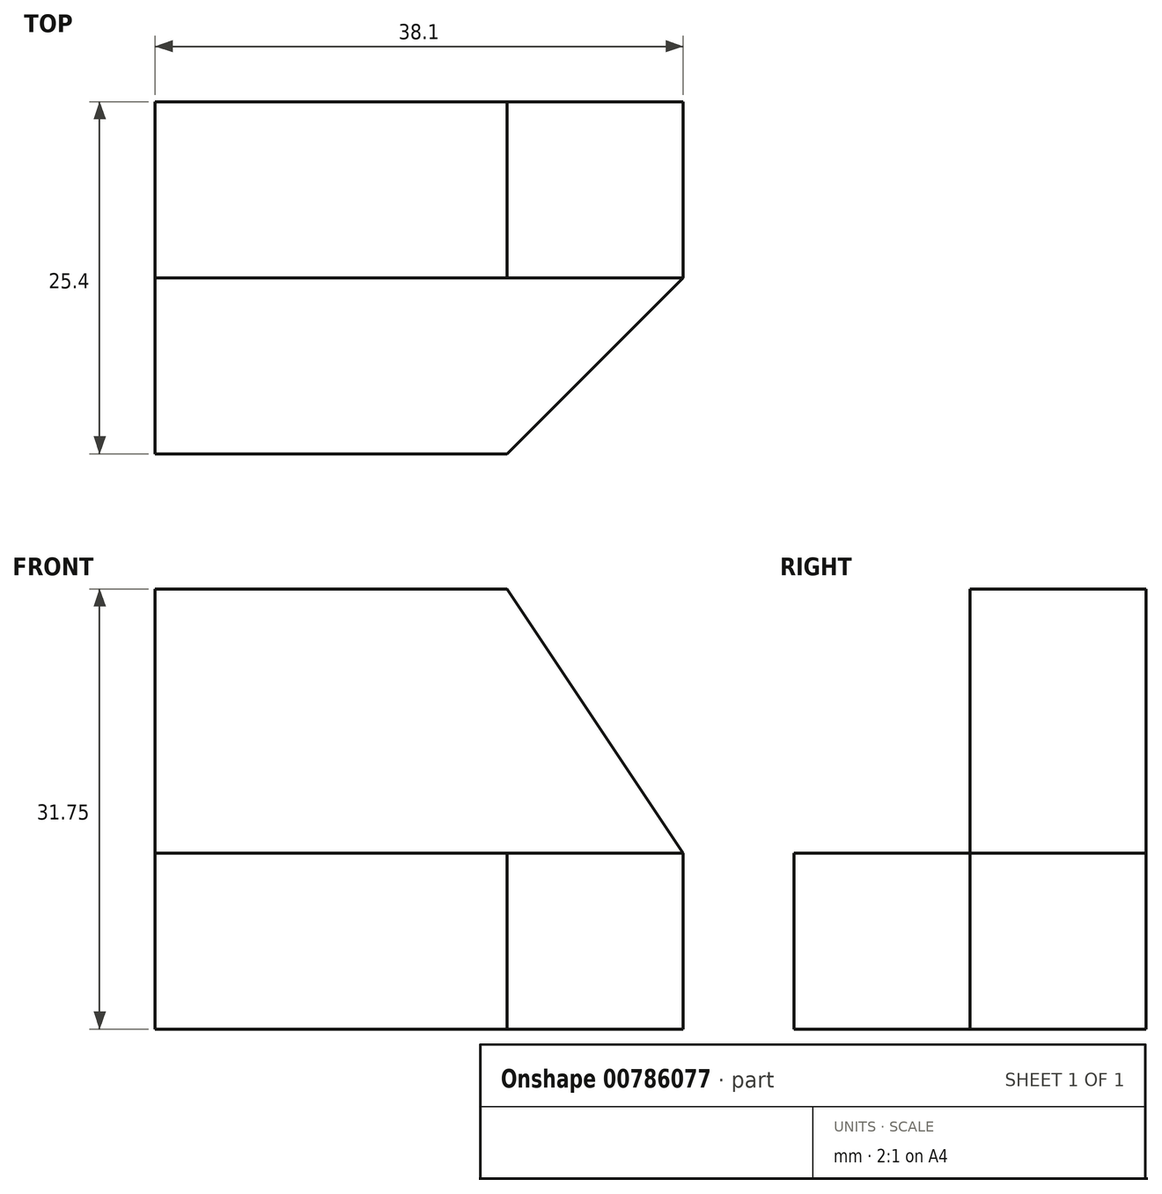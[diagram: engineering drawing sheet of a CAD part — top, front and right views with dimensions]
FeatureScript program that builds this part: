
annotation { "Feature Type Name" : "Feature", "Feature Type Description" : "" }
export const myFeature = defineFeature(function(context is Context, id is Id, definition is map)
    precondition{}
    {
        {
            var Q0;
            Q0=qCreatedBy(makeId("Front.planeOp"),FACE);
            var sketch = newSketch(context, id + "F0", { "sketchPlane" : qUnion([Q0])});
            skLineSegment(sketch, "E0", {"start": v(0, 0) * mm, "end": v(38.1, 0) * mm});
            skLineSegment(sketch, "E1", {"start": v(38.1, 0) * mm, "end": v(38.1, 31.75) * mm});
            skLineSegment(sketch, "E2", {"start": v(38.1, 31.75) * mm, "end": v(0, 31.75) * mm});
            skLineSegment(sketch, "E3", {"start": v(0, 31.75) * mm, "end": v(0, 0) * mm});
            skSolve(sketch);
        }
        {
            var Q0;
            Q0=makeQuery(id+"F0.imprint","IMPRINT",FACE,{"disambiguationData":[TD([[makeQuery(id+"F0.imprint","IMPRINT",EDGE,{"derivedFrom":sQuery(id+"F0.wireOp",EDGE,"E0")}),1.0]])]});
            extrude(context, id + "F1", {"entities" : qUnion([Q0]), "depth" : 25.4 * mm, "offsetDistance" : 25.4 * mm});
        }
        {
            var Q0;
            Q0=makeQuery(id+"F1.opExtrude","SWEPT_FACE",FACE,{"disambiguationData":[OSD([sQuery(id+"F0.wireOp",EDGE,"E1")])]});
            var sketch = newSketch(context, id + "F2", { "sketchPlane" : qUnion([Q0])});
            skLineSegment(sketch, "E4", {"start": v(-25.4, 0) * mm, "end": v(-25.4, 12.7) * mm});
            skLineSegment(sketch, "E5", {"start": v(-25.4, 12.7) * mm, "end": v(-12.7, 12.7) * mm});
            skLineSegment(sketch, "E6", {"start": v(-12.7, 12.7) * mm, "end": v(-12.7, 31.75) * mm});
            skSolve(sketch);
        }
        {
            var Q0;
            {var subQ0=sQuery(id+"F2.wireOp",EDGE,"E5");Q0=makeQuery(id+"F2.imprint","IMPRINT",FACE,{"disambiguationData":[TD([[makeQuery(id+"F2.imprint","IMPRINT",EDGE,{"derivedFrom":subQ0}),1.0]])]});}
            extrude(context, id + "F3", {"entities" : qUnion([Q0]), "operationType" : NewBodyOperationType.REMOVE, "oppositeDirection" : true, "depth" : 38.1 * mm, "offsetDistance" : 25.4 * mm});
        }
        {
            var Q0;
            Q0=makeQuery(id+"F3.boolean.opBoolean","COPY",FACE,{"derivedFrom":makeQuery(id+"F3.opExtrude","SWEPT_FACE",FACE,{"disambiguationData":[OSD([sQuery(id+"F2.wireOp",EDGE,"E6")])]})});
            var sketch = newSketch(context, id + "F4", { "sketchPlane" : qUnion([Q0])});
            skLineSegment(sketch, "E7", {"start": v(0, 31.75) * mm, "end": v(25.4, 31.75) * mm});
            skLineSegment(sketch, "E8", {"start": v(25.4, 31.75) * mm, "end": v(38.1, 12.7) * mm});
            skSolve(sketch);
        }
        {
            var Q0;
            {var subQ0=sQuery(id+"F4.wireOp",EDGE,"E8");Q0=makeQuery(id+"F4.imprint","IMPRINT",FACE,{"disambiguationData":[TD([[makeQuery(id+"F4.imprint","IMPRINT",EDGE,{"derivedFrom":subQ0}),1.0]])]});}
            extrude(context, id + "F5", {"entities" : qUnion([Q0]), "operationType" : NewBodyOperationType.REMOVE, "oppositeDirection" : true, "depth" : 12.7 * mm, "offsetDistance" : 25.4 * mm});
        }
        {
            var Q0;
            Q0=makeQuery(id+"F3.boolean.opBoolean","COPY",FACE,{"derivedFrom":makeQuery(id+"F3.opExtrude","SWEPT_FACE",FACE,{"disambiguationData":[OSD([sQuery(id+"F2.wireOp",EDGE,"E5")])]})});
            var sketch = newSketch(context, id + "F6", { "sketchPlane" : qUnion([Q0])});
            skLineSegment(sketch, "E9", {"start": v(38.1, -25.4) * mm, "end": v(25.4, -25.4) * mm});
            skLineSegment(sketch, "E10", {"start": v(25.4, -25.4) * mm, "end": v(38.1, -12.7) * mm});
            skSolve(sketch);
        }
        {
            var Q0;
            Q0=makeQuery(id+"F6.imprint","IMPRINT",FACE,{"disambiguationData":[TD([[makeQuery(id+"F6.imprint","IMPRINT",EDGE,{"derivedFrom":sQuery(id+"F6.wireOp",EDGE,"E9")}),1.0]])]});
            extrude(context, id + "F7", {"entities" : qUnion([Q0]), "operationType" : NewBodyOperationType.REMOVE, "oppositeDirection" : true, "depth" : 12.7 * mm, "offsetDistance" : 25.4 * mm});
        }
    });
